# Revit family: R-MVF-0001
name_source: partatom
category: Portes
units: mm (PartAtom-declared; Revit-internal decimal feet)

## family parameters
Couper avec des vides une fois chargée = Non
Hôte = Mur
Partagée = Non
Point de calcul de pièce = Oui
Toujours verticalement = Oui

## types (1)
- MVF-0001
    ----- EQUIPEMENTS ----------------------- = .
    ----- PARAMETRES DE L'HÔTE -------------------- = .
    ----- PARAMETRES DES VANTAUX -------------------- = .
    ----- PARAMETRES POSITION HUISSERIE -------------------- = .
    ----- PARAMETRES PROFIL HUISSERIE -------------------- = .
    ----- TYPE DE PARCLOSAGE -------------------- = .
    ----- TYPE DE VANTAIL -------------------- = .
    ------INUTILISES-------------------------- = .
    ----PARAMETRES INUTILISES------------------------- = .
    1 Vantail = Oui
    2 Vantaux = Non
    Coloris Verre = Verre
    Construction analytique = <Aucun>
    DAS = Non
    Description = Bloc-porte vitré RESISTANT AU FEU 1 vantail, simple action, EW30, avec cadre et parcloses bois, sur huisserie bois
    Désaffleurement_Vantail = 4 mm  [stored 0.0131234 ft]
    Epaisseur joint = 4 mm  [stored 0.0131234 ft]
    Epaisseurs_Vantaux = 56 mm  [stored 0.183727 ft]
    FDES Inies = https://www.base-inies.fr
    Fabricant = MALERBA
    Fiche_Produit = MVF-0001
    Fonction = Intérieur
    Hauteur axe ventouse = 70 mm  [stored 0.229659 ft]
    Hauteur_Axe_Bequille = 1045 mm  [stored 3.42848 ft]
    Hauteur_Vantaux_Souhaitée = 2040 mm  [stored 6.69291 ft]
    Jeu_Côté_Articulation_Vantail = 2 mm  [stored 0.00656168 ft]
    Jeu_Côté_Fermeture_Vantail = 3 mm  [stored 0.00984252 ft]
    Jeu_Traverse_Basse_Vantail = 7 mm  [stored 0.0229659 ft]
    Jeu_Traverse_Haute_Vantail = 3 mm  [stored 0.00984252 ft]
    Largeur Feuillure Battement Articulation = 15 mm  [stored 0.0492126 ft]
    Largeur parclose = 23 mm  [stored 0.0754593 ft]
    Largeur parclose recouvrement = 12 mm  [stored 0.0393701 ft]
    Largeur_Axe_Bequille = 50 mm  [stored 0.164042 ft]
    Largeur_Feuillure_Battement_Semi_Fixe = 15 mm  [stored 0.0492126 ft]
    Largeur_Feuillure_Battement_Service = 15 mm  [stored 0.0492126 ft]
    Largeur_Feuillure_Profil = 15 mm  [stored 0.0492126 ft]
    Largeur_Vantail_Semi_Fixe_Souhaitée = 630 mm  [stored 2.06693 ft]
    Largeur_Vantail_Service_Souhaitée = 930 mm  [stored 3.05118 ft]
    Materiaux_Dominant = Bois
    Modèle = 43 - SA-HB
    Note d'identification = 1V EW30 VITRE
    Parclosage Double = Non
    Parclosage Simple Coté Opposé Paumelles = Non
    Parclosage Simple Coté Paumelles = Oui
    Parclosage à Recouvrement = Non
    Paumelle Décalage Largeur Axe = 1 mm  [stored 0.00328084 ft]
    Paumelle Décalage Profondeur Axe = 8 mm  [stored 0.0262467 ft]
    Paumelle Position Largeur Axe = 0 mm  [stored 0 ft]
    Paumelle Position Profondeur Axe = 8 mm  [stored 0.0262467 ft]
    Paumelle_1 = 250 mm  [stored 0.82021 ft]
    Paumelle_2 = 1075 mm
    Paumelle_3 = 1750 mm  [stored 5.74147 ft]
    Paumelle_4 = 1900 mm  [stored 6.2336 ft]
    Paumelle_5 = 500 mm  [stored 1.64042 ft]
    Profondeur Feuillure Battement Articulation = 15 mm  [stored 0.0492126 ft]
    Profondeur parclose = 18 mm  [stored 0.0590551 ft]
    Profondeur parclose recouvrement = 7 mm  [stored 0.0229659 ft]
    Profondeur_Feuillure_Battement_Semi_Fixe = 17 mm
    Profondeur_Feuillure_Battement_Service = 41 mm  [stored 0.134514 ft]
    Profondeur_Feuillure_Profil = 47 mm  [stored 0.154199 ft]
    Reference_Commerciale = 1V GV SA30
    Reprise_Doublage_1 = 30 mm  [stored 0.0984252 ft]
    Reprise_Doublage_2 = 30 mm  [stored 0.0984252 ft]
    Reprise_Doublage_Haut = 30 mm  [stored 0.0984252 ft]
    Resistance_Feu = E30-EW30
    Sens_Feu = Recto / Verso
    Thermique (W/m2.°K) = 0
    URL = https://www.malerba.fr
    Ventouse = Non
    Ventouse Position Largeur Axe = 60 mm  [stored 0.19685 ft]
    Visibilité poignée = Oui
    Vitrage Epaisseur = 9 mm  [stored 0.0295276 ft]
    X_Largeur_Feuillure_Battement_Service = 15 mm  [stored 0.0492126 ft]

note: [stored X ft] marks values corroborated as IEEE doubles in the binary element streams (Revit-internal decimal feet)

## geometry (parser evidence)
native form markers: Blend x12
no freeform markers — native parametric forms only
